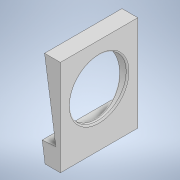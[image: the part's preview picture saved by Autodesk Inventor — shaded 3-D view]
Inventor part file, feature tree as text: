
AUTODESK INVENTOR PART (.ipt)
format: ipt  version: 2021.1 (Build 251245000, 245)  size: 1,212,928 bytes
history: native  units: in
note: dims shown in document units (in); Inventor stores cm internally (conversion verified against a paired STEP export)
features: extrude x4, sketch x4, fillet x1, split x1
ambient origin geometry x8: Origin, YZ Plane, XZ Plane, XY Plane, X Axis, Y Axis, Z Axis, Center Point
bodies: Body1 (feature_tree)
feature tree (10):
  extrude  "Extrusion7"  Depth=0.695in
  extrude  "Extrusion8"  Depth=0.0344in
  extrude  "Extrusion11"  Depth=0.2in
  fillet  "Fillet1"  Radius=3.4in
  extrude  "Extrusion12"  Depth=0.2in
  split  "Split6"
  sketch  "Sketch6"  dims[d31=3.3in d32=0.695in]
  sketch  "Sketch7"  dims[d33=0.9in d35=0.0344in]
  sketch  "Sketch11"  dims[d36=0.0in d37=0.2in d38=3.4in d39=0.0in]
  sketch  "Sketch12"  dims[d40=2.5in d41=0.2in d42=0.0in d43=0.0in d47=0.8in d50=0.05in d51=0.0in d52=0.0625in d53=0.05in d54=0.0in]
